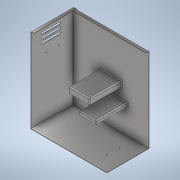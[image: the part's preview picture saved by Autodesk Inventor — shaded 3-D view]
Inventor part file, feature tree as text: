
AUTODESK INVENTOR PART (.ipt)
format: ipt  version: 2021 (Build 250183000, 183)  size: 282,624 bytes
history: native  units: mm
features: other x14, sketch x9, sheet_metal_op x5, extrude x4, fillet x1
ambient origin geometry x8: Origin, YZ Plane, XZ Plane, XY Plane, X Axis, Y Axis, Z Axis, Center Point
bodies: Body1 (feature_tree)
feature tree (33):
  other  "Sólido1"
  sheet_metal_op  "Face1"
  sheet_metal_op  "Flange1"
  sheet_metal_op  "Flange2"
  sheet_metal_op  "Flange3"
  sheet_metal_op  "Flange4"
  extrude  "Extrusão1"  Depth=400.0mm
  fillet  "Arredondamento1"  Radius=1.5mm
  extrude  "Extrusão2"  Depth=0.75mm
  extrude  "Extrusão3"  Depth=1.5mm
  extrude  "Extrusão4"  Depth=1.5mm
  sketch  "Esboço1"  dims[d0=360.0mm d1=400.0mm d2=1.5mm]
  other  "Placa1"
  sketch  "Esboço2"  dims[d3=1.5mm d4=0.75mm]
  other  "Placa2"
  other  "Vergadura1"
  other  "Canto1"
  sketch  "Esboço3"  dims[d5=3.0mm d6=1.5mm]
  other  "Placa3"
  other  "Vergadura2"
  other  "Canto2"
  sketch  "Esboço4"  dims[d7=200.0mm d8=90.0deg d9=1.5mm d10=6.0mm]
  other  "Placa4"
  other  "Vergadura3"
  other  "Canto3"
  sketch  "Esboço5"  dims[d11=1.5mm]
  other  "Placa5"
  other  "Vergadura4"
  other  "Canto4"
  sketch  "Esboço6"  dims[d12=1.5mm]
  sketch  "Esboço7"  dims[d13=1.5mm]
  sketch  "Esboço8"  dims[d14=0.75mm]
  sketch  "Esboço9"  dims[d15=3.0mm d16=1.5mm d17=200.0mm d18=90.0deg d19=1.5mm d20=6.0mm d21=1.5mm d22=1.5mm d23=1.5mm d24=0.75mm d25=3.0mm d26=1.5mm d27=15.0mm d28=90.0deg d29=1.5mm d30=6.0mm d31=1.5mm d32=1.5mm d33=1.5mm d34=0.75mm d35=3.0mm d36=1.5mm d37=15.0mm d38=0.0mm d39=15.0mm d40=90.0deg d41=1.5mm d42=6.0mm d43=1.5mm d44=1.5mm d45=100.0mm d46=30.0mm d47=80.0mm d48=20.0mm d49=60.0mm d50=150.0mm d51=0.0mm d52=4.0mm d53=10.0mm d54=40.0mm d55=30.0mm d56=10.0mm d57=10.0mm d58=20.0mm d59=20.0mm d60=150.0mm d61=0.0mm d62=3.0mm d63=3.0mm d64=70.0mm d65=60.0mm d66=120.0mm d67=5.0mm d68=0.0mm d69=3.0mm d70=3.0mm d71=70.0mm d72=60.0mm d73=70.0mm d74=5.0mm d75=0.0mm]
